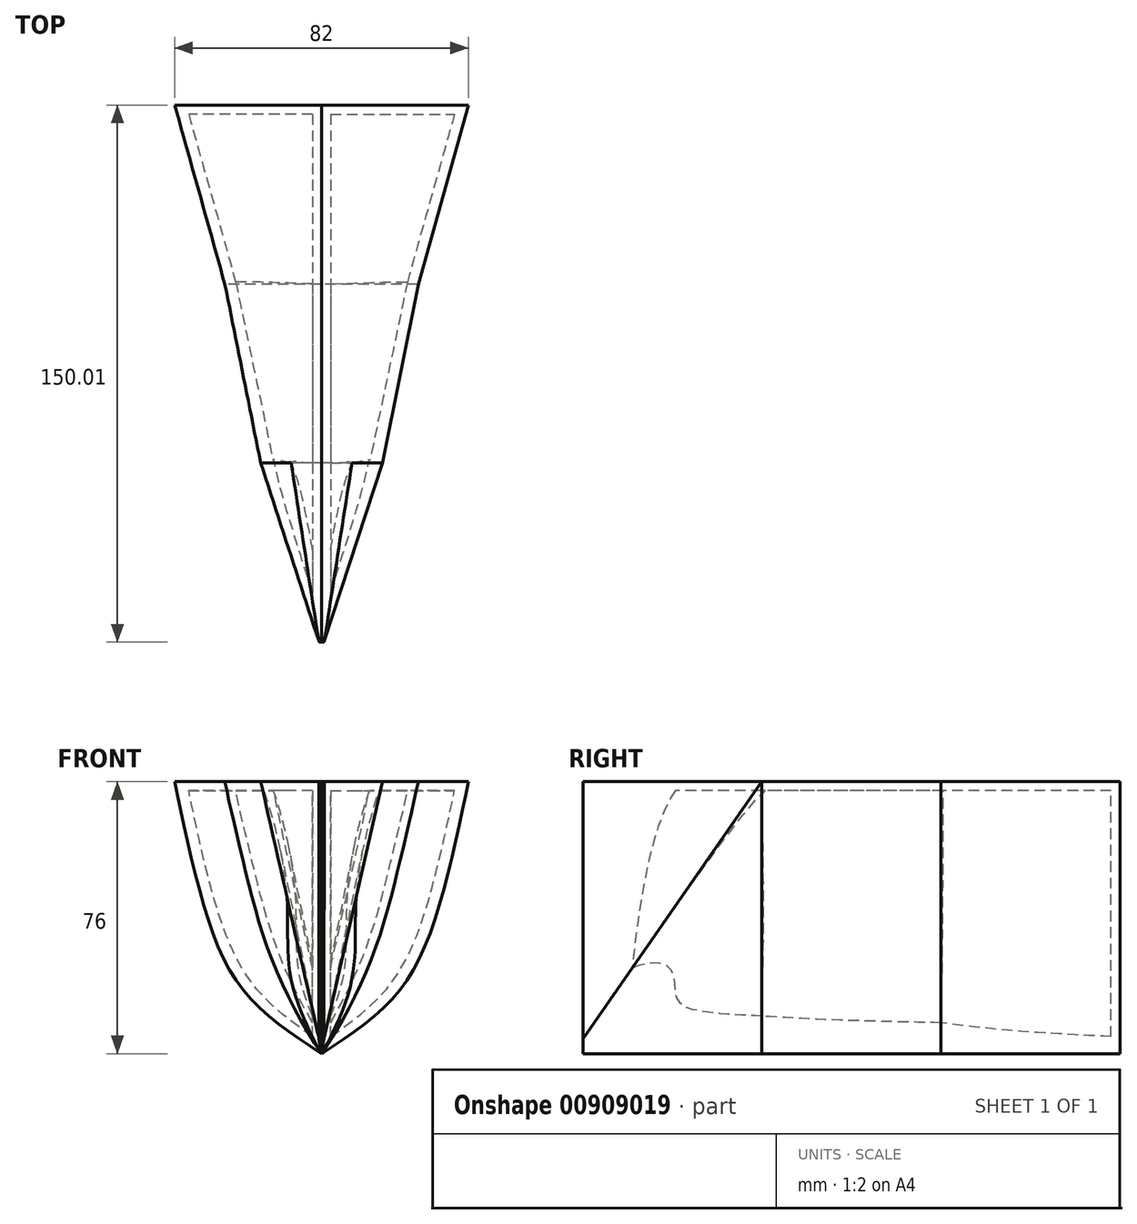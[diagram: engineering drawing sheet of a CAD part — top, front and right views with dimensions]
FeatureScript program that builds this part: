
annotation { "Feature Type Name" : "Feature", "Feature Type Description" : "" }
export const myFeature = defineFeature(function(context is Context, id is Id, definition is map)
    precondition{}
    {
        {
            var Q0;
            Q0=qCreatedBy(makeId("Front.planeOp"),FACE);
            var sketch = newSketch(context, id + "F0", { "sketchPlane" : qUnion([Q0])});
            skLineSegment(sketch, "E0", {"start": v(0, 0) * mm, "end": v(0, 76) * mm});
            skLineSegment(sketch, "E1", {"start": v(0, 76) * mm, "end": v(17, 76) * mm});
            skFitSpline(sketch, "E2", {"points": [v(17, 76) * mm, v(9.77, 45.12) * mm, v(7.96, 18.5) * mm, v(0, 0) * mm], "startDerivative": vector(-25.36, -64.7) * mm, "endDerivative": vector(-12.13, -18.2) * mm});
            skSolve(sketch);
        }
        {
            var Q0;
            Q0=makeQuery(id+"F0.imprint","IMPRINT",FACE,{"disambiguationData":[TD([[makeQuery(id+"F0.imprint","IMPRINT",EDGE,{"derivedFrom":sQuery(id+"F0.wireOp",EDGE,"E0")}),-1.0]])]});
            extrude(context, id + "F1", {"entities" : qUnion([Q0]), "depth" : 0 * mm, "offsetDistance" : 25 * mm});
        }
        {
            var Q0;
            Q0=qCreatedBy(makeId("Front.planeOp"),FACE);
            cPlane(context, id + "F2", {"entities" : qUnion([Q0]), "cplaneType" : CPlaneType.OFFSET, "offset" : 50 * mm, "width" : 150 * mm, "height" : 150 * mm});
        }
        {
            var Q0;
            Q0=qCreatedBy(id+"F2.planeOp",FACE);
            var sketch = newSketch(context, id + "F3", { "sketchPlane" : qUnion([Q0])});
            skLineSegment(sketch, "E3", {"start": v(0, 0) * mm, "end": v(0.69, 4.15) * mm});
            skLineSegment(sketch, "E4", {"start": v(0.69, 4.15) * mm, "end": v(0.75, 76) * mm});
            skLineSegment(sketch, "E5", {"start": v(0.75, 76) * mm, "end": v(0, 76) * mm});
            skLineSegment(sketch, "E6", {"start": v(0, 76) * mm, "end": v(0, 0) * mm});
            skSolve(sketch);
        }
        {
            var Q0;
            Q0=makeQuery(id+"F3.imprint","IMPRINT",FACE,{"disambiguationData":[TD([[makeQuery(id+"F3.imprint","IMPRINT",EDGE,{"derivedFrom":sQuery(id+"F3.wireOp",EDGE,"E3")}),1.0]])]});
            extrude(context, id + "F4", {"entities" : qUnion([Q0]), "depth" : 0.01 * mm, "offsetDistance" : 25 * mm});
        }
        {
            var Q0;
            Q0=makeQuery(id+"F1.opExtrude","CAP_FACE",FACE,{"disambiguationData":[OSD([sQuery(id+"F0.wireOp",EDGE,"E0"),sQuery(id+"F0.wireOp",EDGE,"E1"),sQuery(id+"F0.wireOp",EDGE,"E2")])],"isStart":false});
            var Q1;
            Q1=makeQuery(id+"F4.opExtrude","CAP_FACE",FACE,{"disambiguationData":[OSD([sQuery(id+"F3.wireOp",EDGE,"E3"),sQuery(id+"F3.wireOp",EDGE,"E4"),sQuery(id+"F3.wireOp",EDGE,"E5"),sQuery(id+"F3.wireOp",EDGE,"E6")])],"isStart":true});
            loft(context, id + "F5", {"sheetProfilesArray" : [{ "sheetProfileEntities" : qUnion([Q0]) }, { "sheetProfileEntities" : qUnion([Q1]) }]});
        }
        {
            var Q0;
            Q0=qCreatedBy(makeId("Front.planeOp"),FACE);
            cPlane(context, id + "F6", {"entities" : qUnion([Q0]), "cplaneType" : CPlaneType.OFFSET, "offset" : 50 * mm, "oppositeDirection" : true, "width" : 150 * mm, "height" : 150 * mm});
        }
        {
            var Q0;
            Q0=qCreatedBy(id+"F6.planeOp",FACE);
            var sketch = newSketch(context, id + "F7", { "sketchPlane" : qUnion([Q0])});
            skLineSegment(sketch, "E7", {"start": v(0, 0) * mm, "end": v(0, 76) * mm});
            skLineSegment(sketch, "E8", {"start": v(0, 76) * mm, "end": v(27, 76) * mm});
            skFitSpline(sketch, "E9", {"points": [v(27, 76) * mm, v(22, 54.23) * mm, v(14.03, 26.66) * mm, v(0, 0) * mm], "startDerivative": vector(-11.37, -55.97) * mm, "endDerivative": vector(-46.16, -68.27) * mm});
            skSolve(sketch);
        }
        {
            var Q1;
            Q1=makeQuery(id+"F7.imprint","IMPRINT",FACE,{"disambiguationData":[TD([[makeQuery(id+"F7.imprint","IMPRINT",EDGE,{"derivedFrom":sQuery(id+"F7.wireOp",EDGE,"E7")}),-1.0]])]});
            var Q2;
            Q2=makeQuery(id+"F0.imprint","IMPRINT",FACE,{"disambiguationData":[TD([[makeQuery(id+"F0.imprint","IMPRINT",EDGE,{"derivedFrom":sQuery(id+"F0.wireOp",EDGE,"E0")}),-1.0]])]});
            loft(context, id + "F8", {"operationType" : NewBodyOperationType.ADD, "sheetProfilesArray" : [{ "sheetProfileEntities" : qUnion([Q1]) }, { "sheetProfileEntities" : qUnion([Q2]) }]});
        }
        {
            var Q0;
            Q0=qCreatedBy(id+"F6.planeOp",FACE);
            cPlane(context, id + "F9", {"entities" : qUnion([Q0]), "cplaneType" : CPlaneType.OFFSET, "offset" : 50 * mm, "oppositeDirection" : true, "width" : 150 * mm, "height" : 150 * mm});
        }
        {
            var Q0;
            Q0=qCreatedBy(id+"F9.planeOp",FACE);
            var sketch = newSketch(context, id + "F10", { "sketchPlane" : qUnion([Q0])});
            skLineSegment(sketch, "E10", {"start": v(0, 0) * mm, "end": v(0, 76) * mm});
            skLineSegment(sketch, "E11", {"start": v(0, 76) * mm, "end": v(41, 76) * mm});
            skFitSpline(sketch, "E12", {"points": [v(41, 76) * mm, v(31.99, 38.45) * mm, v(19.8, 15.3) * mm, v(0, 0) * mm], "startDerivative": vector(-17.34, -81.35) * mm, "endDerivative": vector(-70.37, -46.1) * mm});
            skSolve(sketch);
        }
        {
            var Q1;
            Q1=makeQuery(id+"F10.imprint","IMPRINT",FACE,{"disambiguationData":[TD([[makeQuery(id+"F10.imprint","IMPRINT",EDGE,{"derivedFrom":sQuery(id+"F10.wireOp",EDGE,"E10")}),-1.0]])]});
            var Q2;
            Q2=makeQuery(id+"F8.opLoft","CAP_FACE",FACE,{"disambiguationData":[OSD([makeQuery(id+"F7.imprint","IMPRINT",FACE,{"disambiguationData":[TD([[makeQuery(id+"F7.imprint","IMPRINT",EDGE,{"derivedFrom":sQuery(id+"F7.wireOp",EDGE,"E7")}),-1.0]])]})])],"isStart":true});
            loft(context, id + "F11", {"operationType" : NewBodyOperationType.ADD, "sheetProfilesArray" : [{ "sheetProfileEntities" : qUnion([Q1]) }, { "sheetProfileEntities" : qUnion([Q2]) }]});
        }
        {
            var Q0;
            Q0=makeQuery(id+"F1.opExtrude","SWEPT_BODY",BODY,{"disambiguationData":[OSD([sQuery(id+"F0.wireOp",EDGE,"E0"),sQuery(id+"F0.wireOp",EDGE,"E1"),sQuery(id+"F0.wireOp",EDGE,"E2")])]});
            var Q1;
            Q1=makeQuery(id+"F5.opLoft","SWEPT_BODY",BODY,{"disambiguationData":[OSD([sQuery(id+"F0.wireOp",EDGE,"E0"),sQuery(id+"F0.wireOp",EDGE,"E1"),sQuery(id+"F0.wireOp",EDGE,"E2"),sQuery(id+"F3.wireOp",EDGE,"E3"),sQuery(id+"F3.wireOp",EDGE,"E4"),sQuery(id+"F3.wireOp",EDGE,"E5"),sQuery(id+"F3.wireOp",EDGE,"E6")])]});
            var Q2;
            Q2=makeQuery(id+"F4.opExtrude","SWEPT_BODY",BODY,{"disambiguationData":[OSD([sQuery(id+"F3.wireOp",EDGE,"E3"),sQuery(id+"F3.wireOp",EDGE,"E4"),sQuery(id+"F3.wireOp",EDGE,"E5"),sQuery(id+"F3.wireOp",EDGE,"E6")])]});
            var Q3;
            Q3=makeQuery(id+"F5.opLoft","SWEPT_FACE",FACE,{"disambiguationData":[OSD([sQuery(id+"F0.wireOp",EDGE,"E0"),sQuery(id+"F0.wireOp",EDGE,"E1"),sQuery(id+"F0.wireOp",EDGE,"E2"),sQuery(id+"F3.wireOp",EDGE,"E3"),sQuery(id+"F3.wireOp",EDGE,"E5"),sQuery(id+"F3.wireOp",EDGE,"E6")])]});
            mirror(context, id + "F12", {"entities" : qUnion([Q0, Q1, Q2]), "mirrorPlane" : qUnion([Q3])});
        }
        {
            var Q0;
            Q0=makeQuery(id+"F11.opLoft","CAP_FACE",FACE,{"disambiguationData":[OSD([makeQuery(id+"F10.imprint","IMPRINT",FACE,{"disambiguationData":[TD([[makeQuery(id+"F10.imprint","IMPRINT",EDGE,{"derivedFrom":sQuery(id+"F10.wireOp",EDGE,"E10")}),-1.0]])]})])],"isStart":true});
            var Q1;
            {var subQ0=sQuery(id+"F10.wireOp",EDGE,"E12");var subQ1=sQuery(id+"F10.wireOp",EDGE,"E11");var subQ2=sQuery(id+"F10.wireOp",EDGE,"E10");var subQ3=sQuery(id+"F7.wireOp",EDGE,"E9");var subQ4=sQuery(id+"F7.wireOp",EDGE,"E8");var subQ5=sQuery(id+"F7.wireOp",EDGE,"E7");Q1=makeQuery(id+"F11.opLoft","SWEPT_FACE",FACE,{"disambiguationData":[OSD([subQ5,subQ4,subQ3,subQ2,subQ1,subQ0]),TDD([makeQuery(id+"F8.opLoft","MID_CAP_VERTEX",VERTEX,{"disambiguationData":[OSD([subQ5,subQ3])],"capPos":0.0}),makeQuery(id+"F8.opLoft","MID_CAP_VERTEX",VERTEX,{"disambiguationData":[OSD([subQ4,subQ3])],"capPos":0.0}),makeQuery(id+"F8.opLoft","MID_CAP_EDGE",EDGE,{"disambiguationData":[OSD([subQ5,subQ4,subQ3]),TDD([makeQuery(id+"F7.imprint","INTERSECT",VERTEX,{"derivedFrom":[subQ5,subQ3]}),makeQuery(id+"F7.imprint","INTERSECT",VERTEX,{"derivedFrom":[subQ4,subQ3]}),makeQuery(id+"F7.imprint","IMPRINT",EDGE,{"derivedFrom":subQ3})])],"capPos":0.0}),makeQuery(id+"F10.imprint","INTERSECT",VERTEX,{"derivedFrom":[subQ2,subQ0]}),makeQuery(id+"F10.imprint","INTERSECT",VERTEX,{"derivedFrom":[subQ1,subQ0]}),makeQuery(id+"F10.imprint","IMPRINT",EDGE,{"derivedFrom":subQ0})])]});}
            var Q2;
            {var subQ0=sQuery(id+"F7.wireOp",EDGE,"E9");var subQ1=sQuery(id+"F7.wireOp",EDGE,"E8");var subQ2=sQuery(id+"F7.wireOp",EDGE,"E7");var subQ3=sQuery(id+"F0.wireOp",EDGE,"E2");var subQ4=sQuery(id+"F0.wireOp",EDGE,"E1");var subQ5=sQuery(id+"F0.wireOp",EDGE,"E0");Q2=makeQuery(id+"F8.opLoft","SWEPT_FACE",FACE,{"disambiguationData":[OSD([subQ5,subQ4,subQ3,subQ2,subQ1,subQ0]),TDD([makeQuery(id+"F0.imprint","INTERSECT",VERTEX,{"derivedFrom":[subQ5,subQ3]}),makeQuery(id+"F0.imprint","INTERSECT",VERTEX,{"derivedFrom":[subQ4,subQ3]}),makeQuery(id+"F0.imprint","IMPRINT",EDGE,{"derivedFrom":subQ3}),makeQuery(id+"F7.imprint","INTERSECT",VERTEX,{"derivedFrom":[subQ2,subQ0]}),makeQuery(id+"F7.imprint","INTERSECT",VERTEX,{"derivedFrom":[subQ1,subQ0]}),makeQuery(id+"F7.imprint","IMPRINT",EDGE,{"derivedFrom":subQ0})])]});}
            var Q3;
            {var subQ0=sQuery(id+"F10.wireOp",EDGE,"E11");var subQ1=sQuery(id+"F10.wireOp",EDGE,"E12");var subQ2=sQuery(id+"F10.wireOp",EDGE,"E10");var subQ3=sQuery(id+"F7.wireOp",EDGE,"E8");var subQ4=makeQuery(id+"F7.imprint","IMPRINT",EDGE,{"derivedFrom":subQ3});var subQ5=sQuery(id+"F7.wireOp",EDGE,"E9");var subQ6=makeQuery(id+"F7.imprint","INTERSECT",VERTEX,{"derivedFrom":[subQ3,subQ5]});var subQ7=sQuery(id+"F7.wireOp",EDGE,"E7");var subQ8=makeQuery(id+"F7.imprint","INTERSECT",VERTEX,{"derivedFrom":[subQ7,subQ3]});var subQ9=sQuery(id+"F0.wireOp",EDGE,"E1");var subQ10=sQuery(id+"F0.wireOp",EDGE,"E2");var subQ11=sQuery(id+"F0.wireOp",EDGE,"E0");Q3=makeQuery(id+"F11.boolean.opBoolean","MERGE",FACE,{"derivedFrom":[makeQuery(id+"F8.boolean.opBoolean","MERGE",FACE,{"derivedFrom":[makeQuery(id+"F1.opExtrude","SWEPT_FACE",FACE,{"disambiguationData":[OSD([subQ9])]}),makeQuery(id+"F8.opLoft","SWEPT_FACE",FACE,{"disambiguationData":[OSD([subQ11,subQ9,subQ10,subQ7,subQ3,subQ5]),TDD([makeQuery(id+"F0.imprint","INTERSECT",VERTEX,{"derivedFrom":[subQ11,subQ9]}),makeQuery(id+"F0.imprint","INTERSECT",VERTEX,{"derivedFrom":[subQ9,subQ10]}),makeQuery(id+"F0.imprint","IMPRINT",EDGE,{"derivedFrom":subQ9}),subQ8,subQ6,subQ4])]})]}),makeQuery(id+"F11.opLoft","SWEPT_FACE",FACE,{"disambiguationData":[OSD([subQ7,subQ3,subQ5,subQ2,subQ0,subQ1]),TDD([makeQuery(id+"F8.opLoft","MID_CAP_VERTEX",VERTEX,{"disambiguationData":[OSD([subQ7,subQ3])],"capPos":0.0}),makeQuery(id+"F8.opLoft","MID_CAP_VERTEX",VERTEX,{"disambiguationData":[OSD([subQ3,subQ5])],"capPos":0.0}),makeQuery(id+"F8.opLoft","MID_CAP_EDGE",EDGE,{"disambiguationData":[OSD([subQ7,subQ3,subQ5]),TDD([subQ8,subQ6,subQ4])],"capPos":0.0}),makeQuery(id+"F10.imprint","INTERSECT",VERTEX,{"derivedFrom":[subQ2,subQ0]}),makeQuery(id+"F10.imprint","INTERSECT",VERTEX,{"derivedFrom":[subQ0,subQ1]}),makeQuery(id+"F10.imprint","IMPRINT",EDGE,{"derivedFrom":subQ0})])]})]});}
            var Q4;
            Q4=makeQuery(id+"F5.opLoft","SWEPT_FACE",FACE,{"disambiguationData":[OSD([sQuery(id+"F0.wireOp",EDGE,"E0"),sQuery(id+"F0.wireOp",EDGE,"E1"),sQuery(id+"F0.wireOp",EDGE,"E2"),sQuery(id+"F3.wireOp",EDGE,"E4"),sQuery(id+"F3.wireOp",EDGE,"E5"),sQuery(id+"F3.wireOp",EDGE,"E6")])]});
            var Q5;
            Q5=makeQuery(id+"F5.opLoft","SWEPT_FACE",FACE,{"disambiguationData":[OSD([sQuery(id+"F0.wireOp",EDGE,"E1"),sQuery(id+"F0.wireOp",EDGE,"E2"),sQuery(id+"F3.wireOp",EDGE,"E3"),sQuery(id+"F3.wireOp",EDGE,"E4"),sQuery(id+"F3.wireOp",EDGE,"E5"),sQuery(id+"F3.wireOp",EDGE,"E6")])]});
            var Q6;
            Q6=makeQuery(id+"F12.opPattern","COPY",FACE,{"derivedFrom":makeQuery(id+"F11.opLoft","CAP_FACE",FACE,{"disambiguationData":[OSD([makeQuery(id+"F10.imprint","IMPRINT",FACE,{"disambiguationData":[TD([[makeQuery(id+"F10.imprint","IMPRINT",EDGE,{"derivedFrom":sQuery(id+"F10.wireOp",EDGE,"E10")}),-1.0]])]})])],"isStart":true}),"instanceName":"1"});
            var Q7;
            {var subQ0=sQuery(id+"F7.wireOp",EDGE,"E9");var subQ1=sQuery(id+"F7.wireOp",EDGE,"E8");var subQ2=sQuery(id+"F7.wireOp",EDGE,"E7");var subQ3=sQuery(id+"F0.wireOp",EDGE,"E2");var subQ4=sQuery(id+"F0.wireOp",EDGE,"E1");var subQ5=sQuery(id+"F0.wireOp",EDGE,"E0");Q7=makeQuery(id+"F12.opPattern","COPY",FACE,{"derivedFrom":makeQuery(id+"F8.opLoft","SWEPT_FACE",FACE,{"disambiguationData":[OSD([subQ5,subQ4,subQ3,subQ2,subQ1,subQ0]),TDD([makeQuery(id+"F0.imprint","INTERSECT",VERTEX,{"derivedFrom":[subQ5,subQ3]}),makeQuery(id+"F0.imprint","INTERSECT",VERTEX,{"derivedFrom":[subQ4,subQ3]}),makeQuery(id+"F0.imprint","IMPRINT",EDGE,{"derivedFrom":subQ3}),makeQuery(id+"F7.imprint","INTERSECT",VERTEX,{"derivedFrom":[subQ2,subQ0]}),makeQuery(id+"F7.imprint","INTERSECT",VERTEX,{"derivedFrom":[subQ1,subQ0]}),makeQuery(id+"F7.imprint","IMPRINT",EDGE,{"derivedFrom":subQ0})])]}),"instanceName":"1"});}
            var Q8;
            {var subQ0=sQuery(id+"F10.wireOp",EDGE,"E12");var subQ1=sQuery(id+"F10.wireOp",EDGE,"E11");var subQ2=sQuery(id+"F10.wireOp",EDGE,"E10");var subQ3=sQuery(id+"F7.wireOp",EDGE,"E9");var subQ4=sQuery(id+"F7.wireOp",EDGE,"E8");var subQ5=sQuery(id+"F7.wireOp",EDGE,"E7");Q8=makeQuery(id+"F12.opPattern","COPY",FACE,{"derivedFrom":makeQuery(id+"F11.opLoft","SWEPT_FACE",FACE,{"disambiguationData":[OSD([subQ5,subQ4,subQ3,subQ2,subQ1,subQ0]),TDD([makeQuery(id+"F8.opLoft","MID_CAP_VERTEX",VERTEX,{"disambiguationData":[OSD([subQ5,subQ3])],"capPos":0.0}),makeQuery(id+"F8.opLoft","MID_CAP_VERTEX",VERTEX,{"disambiguationData":[OSD([subQ4,subQ3])],"capPos":0.0}),makeQuery(id+"F8.opLoft","MID_CAP_EDGE",EDGE,{"disambiguationData":[OSD([subQ5,subQ4,subQ3]),TDD([makeQuery(id+"F7.imprint","INTERSECT",VERTEX,{"derivedFrom":[subQ5,subQ3]}),makeQuery(id+"F7.imprint","INTERSECT",VERTEX,{"derivedFrom":[subQ4,subQ3]}),makeQuery(id+"F7.imprint","IMPRINT",EDGE,{"derivedFrom":subQ3})])],"capPos":0.0}),makeQuery(id+"F10.imprint","INTERSECT",VERTEX,{"derivedFrom":[subQ2,subQ0]}),makeQuery(id+"F10.imprint","INTERSECT",VERTEX,{"derivedFrom":[subQ1,subQ0]}),makeQuery(id+"F10.imprint","IMPRINT",EDGE,{"derivedFrom":subQ0})])]}),"instanceName":"1"});}
            var Q9;
            Q9=makeQuery(id+"F12.opPattern","COPY",FACE,{"derivedFrom":makeQuery(id+"F1.opExtrude","CAP_FACE",FACE,{"disambiguationData":[OSD([sQuery(id+"F0.wireOp",EDGE,"E0"),sQuery(id+"F0.wireOp",EDGE,"E1"),sQuery(id+"F0.wireOp",EDGE,"E2")])],"isStart":false}),"instanceName":"1"});
            var Q10;
            {var subQ0=sQuery(id+"F10.wireOp",EDGE,"E10");var subQ1=sQuery(id+"F10.wireOp",EDGE,"E11");var subQ2=sQuery(id+"F10.wireOp",EDGE,"E12");var subQ3=sQuery(id+"F7.wireOp",EDGE,"E7");var subQ4=makeQuery(id+"F7.imprint","IMPRINT",EDGE,{"derivedFrom":subQ3});var subQ5=sQuery(id+"F7.wireOp",EDGE,"E8");var subQ6=makeQuery(id+"F7.imprint","INTERSECT",VERTEX,{"derivedFrom":[subQ3,subQ5]});var subQ7=sQuery(id+"F7.wireOp",EDGE,"E9");var subQ8=makeQuery(id+"F7.imprint","INTERSECT",VERTEX,{"derivedFrom":[subQ3,subQ7]});var subQ9=sQuery(id+"F0.wireOp",EDGE,"E0");var subQ10=sQuery(id+"F0.wireOp",EDGE,"E1");var subQ11=sQuery(id+"F0.wireOp",EDGE,"E2");Q10=makeQuery(id+"F12.opPattern","COPY",FACE,{"derivedFrom":makeQuery(id+"F11.boolean.opBoolean","MERGE",FACE,{"derivedFrom":[makeQuery(id+"F8.boolean.opBoolean","MERGE",FACE,{"derivedFrom":[makeQuery(id+"F1.opExtrude","SWEPT_FACE",FACE,{"disambiguationData":[OSD([subQ9])]}),makeQuery(id+"F8.opLoft","SWEPT_FACE",FACE,{"disambiguationData":[OSD([subQ9,subQ10,subQ11,subQ3,subQ5,subQ7]),TDD([makeQuery(id+"F0.imprint","INTERSECT",VERTEX,{"derivedFrom":[subQ9,subQ11]}),makeQuery(id+"F0.imprint","INTERSECT",VERTEX,{"derivedFrom":[subQ9,subQ10]}),makeQuery(id+"F0.imprint","IMPRINT",EDGE,{"derivedFrom":subQ9}),subQ8,subQ6,subQ4])]})]}),makeQuery(id+"F11.opLoft","SWEPT_FACE",FACE,{"disambiguationData":[OSD([subQ3,subQ5,subQ7,subQ0,subQ1,subQ2]),TDD([makeQuery(id+"F8.opLoft","MID_CAP_VERTEX",VERTEX,{"disambiguationData":[OSD([subQ3,subQ7])],"capPos":0.0}),makeQuery(id+"F8.opLoft","MID_CAP_VERTEX",VERTEX,{"disambiguationData":[OSD([subQ3,subQ5])],"capPos":0.0}),makeQuery(id+"F8.opLoft","MID_CAP_EDGE",EDGE,{"disambiguationData":[OSD([subQ3,subQ5,subQ7]),TDD([subQ8,subQ6,subQ4])],"capPos":0.0}),makeQuery(id+"F10.imprint","INTERSECT",VERTEX,{"derivedFrom":[subQ0,subQ2]}),makeQuery(id+"F10.imprint","INTERSECT",VERTEX,{"derivedFrom":[subQ0,subQ1]}),makeQuery(id+"F10.imprint","IMPRINT",EDGE,{"derivedFrom":subQ0})])]})]}),"instanceName":"1"});}
            var Q11;
            {var subQ0=sQuery(id+"F10.wireOp",EDGE,"E11");var subQ1=sQuery(id+"F10.wireOp",EDGE,"E12");var subQ2=sQuery(id+"F10.wireOp",EDGE,"E10");var subQ3=sQuery(id+"F7.wireOp",EDGE,"E8");var subQ4=makeQuery(id+"F7.imprint","IMPRINT",EDGE,{"derivedFrom":subQ3});var subQ5=sQuery(id+"F7.wireOp",EDGE,"E9");var subQ6=makeQuery(id+"F7.imprint","INTERSECT",VERTEX,{"derivedFrom":[subQ3,subQ5]});var subQ7=sQuery(id+"F7.wireOp",EDGE,"E7");var subQ8=makeQuery(id+"F7.imprint","INTERSECT",VERTEX,{"derivedFrom":[subQ7,subQ3]});var subQ9=sQuery(id+"F0.wireOp",EDGE,"E1");var subQ10=sQuery(id+"F0.wireOp",EDGE,"E2");var subQ11=sQuery(id+"F0.wireOp",EDGE,"E0");Q11=makeQuery(id+"F12.opPattern","COPY",FACE,{"derivedFrom":makeQuery(id+"F11.boolean.opBoolean","MERGE",FACE,{"derivedFrom":[makeQuery(id+"F8.boolean.opBoolean","MERGE",FACE,{"derivedFrom":[makeQuery(id+"F1.opExtrude","SWEPT_FACE",FACE,{"disambiguationData":[OSD([subQ9])]}),makeQuery(id+"F8.opLoft","SWEPT_FACE",FACE,{"disambiguationData":[OSD([subQ11,subQ9,subQ10,subQ7,subQ3,subQ5]),TDD([makeQuery(id+"F0.imprint","INTERSECT",VERTEX,{"derivedFrom":[subQ11,subQ9]}),makeQuery(id+"F0.imprint","INTERSECT",VERTEX,{"derivedFrom":[subQ9,subQ10]}),makeQuery(id+"F0.imprint","IMPRINT",EDGE,{"derivedFrom":subQ9}),subQ8,subQ6,subQ4])]})]}),makeQuery(id+"F11.opLoft","SWEPT_FACE",FACE,{"disambiguationData":[OSD([subQ7,subQ3,subQ5,subQ2,subQ0,subQ1]),TDD([makeQuery(id+"F8.opLoft","MID_CAP_VERTEX",VERTEX,{"disambiguationData":[OSD([subQ7,subQ3])],"capPos":0.0}),makeQuery(id+"F8.opLoft","MID_CAP_VERTEX",VERTEX,{"disambiguationData":[OSD([subQ3,subQ5])],"capPos":0.0}),makeQuery(id+"F8.opLoft","MID_CAP_EDGE",EDGE,{"disambiguationData":[OSD([subQ7,subQ3,subQ5]),TDD([subQ8,subQ6,subQ4])],"capPos":0.0}),makeQuery(id+"F10.imprint","INTERSECT",VERTEX,{"derivedFrom":[subQ2,subQ0]}),makeQuery(id+"F10.imprint","INTERSECT",VERTEX,{"derivedFrom":[subQ0,subQ1]}),makeQuery(id+"F10.imprint","IMPRINT",EDGE,{"derivedFrom":subQ0})])]})]}),"instanceName":"1"});}
            var Q12;
            Q12=makeQuery(id+"F12.opPattern","COPY",FACE,{"derivedFrom":makeQuery(id+"F4.opExtrude","CAP_FACE",FACE,{"disambiguationData":[OSD([sQuery(id+"F3.wireOp",EDGE,"E3"),sQuery(id+"F3.wireOp",EDGE,"E4"),sQuery(id+"F3.wireOp",EDGE,"E5"),sQuery(id+"F3.wireOp",EDGE,"E6")])],"isStart":false}),"instanceName":"1"});
            var Q13;
            Q13=makeQuery(id+"F12.opPattern","COPY",FACE,{"derivedFrom":makeQuery(id+"F5.opLoft","SWEPT_FACE",FACE,{"disambiguationData":[OSD([sQuery(id+"F0.wireOp",EDGE,"E0"),sQuery(id+"F0.wireOp",EDGE,"E2"),sQuery(id+"F3.wireOp",EDGE,"E3"),sQuery(id+"F3.wireOp",EDGE,"E4"),sQuery(id+"F3.wireOp",EDGE,"E6")])]}),"instanceName":"1"});
            var Q14;
            Q14=makeQuery(id+"F12.opPattern","COPY",FACE,{"derivedFrom":makeQuery(id+"F5.opLoft","SWEPT_FACE",FACE,{"disambiguationData":[OSD([sQuery(id+"F0.wireOp",EDGE,"E0"),sQuery(id+"F0.wireOp",EDGE,"E1"),sQuery(id+"F0.wireOp",EDGE,"E2"),sQuery(id+"F3.wireOp",EDGE,"E4"),sQuery(id+"F3.wireOp",EDGE,"E5"),sQuery(id+"F3.wireOp",EDGE,"E6")])]}),"instanceName":"1"});
            var Q15;
            Q15=makeQuery(id+"F12.opPattern","COPY",FACE,{"derivedFrom":makeQuery(id+"F5.opLoft","SWEPT_FACE",FACE,{"disambiguationData":[OSD([sQuery(id+"F0.wireOp",EDGE,"E1"),sQuery(id+"F0.wireOp",EDGE,"E2"),sQuery(id+"F3.wireOp",EDGE,"E3"),sQuery(id+"F3.wireOp",EDGE,"E4"),sQuery(id+"F3.wireOp",EDGE,"E5"),sQuery(id+"F3.wireOp",EDGE,"E6")])]}),"instanceName":"1"});
            var Q16;
            Q16=makeQuery(id+"F12.opPattern","COPY",FACE,{"derivedFrom":makeQuery(id+"F5.opLoft","CAP_FACE",FACE,{"disambiguationData":[OSD([sQuery(id+"F0.wireOp",EDGE,"E0"),sQuery(id+"F0.wireOp",EDGE,"E1"),sQuery(id+"F0.wireOp",EDGE,"E2")])],"isStart":true}),"instanceName":"1"});
            var Q17;
            Q17=makeQuery(id+"F1.opExtrude","CAP_FACE",FACE,{"disambiguationData":[OSD([sQuery(id+"F0.wireOp",EDGE,"E0"),sQuery(id+"F0.wireOp",EDGE,"E1"),sQuery(id+"F0.wireOp",EDGE,"E2")])],"isStart":false});
            var Q18;
            {var subQ0=sQuery(id+"F10.wireOp",EDGE,"E10");var subQ1=sQuery(id+"F10.wireOp",EDGE,"E11");var subQ2=sQuery(id+"F10.wireOp",EDGE,"E12");var subQ3=sQuery(id+"F7.wireOp",EDGE,"E7");var subQ4=makeQuery(id+"F7.imprint","IMPRINT",EDGE,{"derivedFrom":subQ3});var subQ5=sQuery(id+"F7.wireOp",EDGE,"E8");var subQ6=makeQuery(id+"F7.imprint","INTERSECT",VERTEX,{"derivedFrom":[subQ3,subQ5]});var subQ7=sQuery(id+"F7.wireOp",EDGE,"E9");var subQ8=makeQuery(id+"F7.imprint","INTERSECT",VERTEX,{"derivedFrom":[subQ3,subQ7]});var subQ9=sQuery(id+"F0.wireOp",EDGE,"E0");var subQ10=sQuery(id+"F0.wireOp",EDGE,"E1");var subQ11=sQuery(id+"F0.wireOp",EDGE,"E2");Q18=makeQuery(id+"F11.boolean.opBoolean","MERGE",FACE,{"derivedFrom":[makeQuery(id+"F8.boolean.opBoolean","MERGE",FACE,{"derivedFrom":[makeQuery(id+"F1.opExtrude","SWEPT_FACE",FACE,{"disambiguationData":[OSD([subQ9])]}),makeQuery(id+"F8.opLoft","SWEPT_FACE",FACE,{"disambiguationData":[OSD([subQ9,subQ10,subQ11,subQ3,subQ5,subQ7]),TDD([makeQuery(id+"F0.imprint","INTERSECT",VERTEX,{"derivedFrom":[subQ9,subQ11]}),makeQuery(id+"F0.imprint","INTERSECT",VERTEX,{"derivedFrom":[subQ9,subQ10]}),makeQuery(id+"F0.imprint","IMPRINT",EDGE,{"derivedFrom":subQ9}),subQ8,subQ6,subQ4])]})]}),makeQuery(id+"F11.opLoft","SWEPT_FACE",FACE,{"disambiguationData":[OSD([subQ3,subQ5,subQ7,subQ0,subQ1,subQ2]),TDD([makeQuery(id+"F8.opLoft","MID_CAP_VERTEX",VERTEX,{"disambiguationData":[OSD([subQ3,subQ7])],"capPos":0.0}),makeQuery(id+"F8.opLoft","MID_CAP_VERTEX",VERTEX,{"disambiguationData":[OSD([subQ3,subQ5])],"capPos":0.0}),makeQuery(id+"F8.opLoft","MID_CAP_EDGE",EDGE,{"disambiguationData":[OSD([subQ3,subQ5,subQ7]),TDD([subQ8,subQ6,subQ4])],"capPos":0.0}),makeQuery(id+"F10.imprint","INTERSECT",VERTEX,{"derivedFrom":[subQ0,subQ2]}),makeQuery(id+"F10.imprint","INTERSECT",VERTEX,{"derivedFrom":[subQ0,subQ1]}),makeQuery(id+"F10.imprint","IMPRINT",EDGE,{"derivedFrom":subQ0})])]})]});}
            var Q19;
            Q19=makeQuery(id+"F5.opLoft","CAP_FACE",FACE,{"disambiguationData":[OSD([sQuery(id+"F0.wireOp",EDGE,"E0"),sQuery(id+"F0.wireOp",EDGE,"E1"),sQuery(id+"F0.wireOp",EDGE,"E2")])],"isStart":true});
            var Q20;
            Q20=makeQuery(id+"F5.opLoft","SWEPT_FACE",FACE,{"disambiguationData":[OSD([sQuery(id+"F0.wireOp",EDGE,"E0"),sQuery(id+"F0.wireOp",EDGE,"E2"),sQuery(id+"F3.wireOp",EDGE,"E3"),sQuery(id+"F3.wireOp",EDGE,"E4"),sQuery(id+"F3.wireOp",EDGE,"E6")])]});
            var Q21;
            Q21=makeQuery(id+"F5.opLoft","SWEPT_FACE",FACE,{"disambiguationData":[OSD([sQuery(id+"F0.wireOp",EDGE,"E0"),sQuery(id+"F0.wireOp",EDGE,"E1"),sQuery(id+"F0.wireOp",EDGE,"E2"),sQuery(id+"F3.wireOp",EDGE,"E3"),sQuery(id+"F3.wireOp",EDGE,"E5"),sQuery(id+"F3.wireOp",EDGE,"E6")])]});
            var Q22;
            Q22=makeQuery(id+"F12.opPattern","COPY",FACE,{"derivedFrom":makeQuery(id+"F4.opExtrude","SWEPT_FACE",FACE,{"disambiguationData":[OSD([sQuery(id+"F3.wireOp",EDGE,"E4")])]}),"instanceName":"1"});
            var Q23;
            Q23=makeQuery(id+"F12.opPattern","COPY",FACE,{"derivedFrom":makeQuery(id+"F5.opLoft","SWEPT_FACE",FACE,{"disambiguationData":[OSD([sQuery(id+"F0.wireOp",EDGE,"E0"),sQuery(id+"F0.wireOp",EDGE,"E1"),sQuery(id+"F0.wireOp",EDGE,"E2"),sQuery(id+"F3.wireOp",EDGE,"E3"),sQuery(id+"F3.wireOp",EDGE,"E5"),sQuery(id+"F3.wireOp",EDGE,"E6")])]}),"instanceName":"1"});
            var Q24;
            Q24=makeQuery(id+"F12.opPattern","COPY",FACE,{"derivedFrom":makeQuery(id+"F4.opExtrude","SWEPT_FACE",FACE,{"disambiguationData":[OSD([sQuery(id+"F3.wireOp",EDGE,"E3")])]}),"instanceName":"1"});
            var Q25;
            Q25=makeQuery(id+"F12.opPattern","COPY",FACE,{"derivedFrom":makeQuery(id+"F5.opLoft","CAP_FACE",FACE,{"disambiguationData":[OSD([sQuery(id+"F3.wireOp",EDGE,"E3"),sQuery(id+"F3.wireOp",EDGE,"E4"),sQuery(id+"F3.wireOp",EDGE,"E5"),sQuery(id+"F3.wireOp",EDGE,"E6")])],"isStart":true}),"instanceName":"1"});
            var Q26;
            Q26=makeQuery(id+"F4.opExtrude","SWEPT_FACE",FACE,{"disambiguationData":[OSD([sQuery(id+"F3.wireOp",EDGE,"E6")])]});
            var Q27;
            Q27=makeQuery(id+"F12.opPattern","COPY",FACE,{"derivedFrom":makeQuery(id+"F4.opExtrude","CAP_FACE",FACE,{"disambiguationData":[OSD([sQuery(id+"F3.wireOp",EDGE,"E3"),sQuery(id+"F3.wireOp",EDGE,"E4"),sQuery(id+"F3.wireOp",EDGE,"E5"),sQuery(id+"F3.wireOp",EDGE,"E6")])],"isStart":true}),"instanceName":"1"});
            var Q28;
            Q28=makeQuery(id+"F12.opPattern","COPY",FACE,{"derivedFrom":makeQuery(id+"F4.opExtrude","SWEPT_FACE",FACE,{"disambiguationData":[OSD([sQuery(id+"F3.wireOp",EDGE,"E6")])]}),"instanceName":"1"});
            var Q29;
            Q29=makeQuery(id+"F4.opExtrude","CAP_FACE",FACE,{"disambiguationData":[OSD([sQuery(id+"F3.wireOp",EDGE,"E3"),sQuery(id+"F3.wireOp",EDGE,"E4"),sQuery(id+"F3.wireOp",EDGE,"E5"),sQuery(id+"F3.wireOp",EDGE,"E6")])],"isStart":true});
            var Q30;
            Q30=makeQuery(id+"F4.opExtrude","CAP_FACE",FACE,{"disambiguationData":[OSD([sQuery(id+"F3.wireOp",EDGE,"E3"),sQuery(id+"F3.wireOp",EDGE,"E4"),sQuery(id+"F3.wireOp",EDGE,"E5"),sQuery(id+"F3.wireOp",EDGE,"E6")])],"isStart":false});
            var Q31;
            Q31=makeQuery(id+"F4.opExtrude","SWEPT_FACE",FACE,{"disambiguationData":[OSD([sQuery(id+"F3.wireOp",EDGE,"E3")])]});
            var Q32;
            Q32=makeQuery(id+"F5.opLoft","CAP_FACE",FACE,{"disambiguationData":[OSD([sQuery(id+"F3.wireOp",EDGE,"E3"),sQuery(id+"F3.wireOp",EDGE,"E4"),sQuery(id+"F3.wireOp",EDGE,"E5"),sQuery(id+"F3.wireOp",EDGE,"E6")])],"isStart":true});
            var Q33;
            Q33=makeQuery(id+"F12.opPattern","COPY",FACE,{"derivedFrom":makeQuery(id+"F4.opExtrude","SWEPT_FACE",FACE,{"disambiguationData":[OSD([sQuery(id+"F3.wireOp",EDGE,"E5")])]}),"instanceName":"1"});
            var Q34;
            Q34=makeQuery(id+"F4.opExtrude","SWEPT_FACE",FACE,{"disambiguationData":[OSD([sQuery(id+"F3.wireOp",EDGE,"E4")])]});
            var Q35;
            Q35=makeQuery(id+"F4.opExtrude","SWEPT_FACE",FACE,{"disambiguationData":[OSD([sQuery(id+"F3.wireOp",EDGE,"E5")])]});
            var Q36;
            Q36=makeQuery(id+"F12.opPattern","COPY",BODY,{"derivedFrom":makeQuery(id+"F1.opExtrude","SWEPT_BODY",BODY,{"disambiguationData":[OSD([sQuery(id+"F0.wireOp",EDGE,"E0"),sQuery(id+"F0.wireOp",EDGE,"E1"),sQuery(id+"F0.wireOp",EDGE,"E2")])]}),"instanceName":"1"});
            var Q37;
            Q37=makeQuery(id+"F1.opExtrude","SWEPT_BODY",BODY,{"disambiguationData":[OSD([sQuery(id+"F0.wireOp",EDGE,"E0"),sQuery(id+"F0.wireOp",EDGE,"E1"),sQuery(id+"F0.wireOp",EDGE,"E2")])]});
            var Q38;
            Q38=makeQuery(id+"F5.opLoft","SWEPT_BODY",BODY,{"disambiguationData":[OSD([sQuery(id+"F0.wireOp",EDGE,"E0"),sQuery(id+"F0.wireOp",EDGE,"E1"),sQuery(id+"F0.wireOp",EDGE,"E2"),sQuery(id+"F3.wireOp",EDGE,"E3"),sQuery(id+"F3.wireOp",EDGE,"E4"),sQuery(id+"F3.wireOp",EDGE,"E5"),sQuery(id+"F3.wireOp",EDGE,"E6")])]});
            var Q39;
            Q39=makeQuery(id+"F12.opPattern","COPY",BODY,{"derivedFrom":makeQuery(id+"F5.opLoft","SWEPT_BODY",BODY,{"disambiguationData":[OSD([sQuery(id+"F0.wireOp",EDGE,"E0"),sQuery(id+"F0.wireOp",EDGE,"E1"),sQuery(id+"F0.wireOp",EDGE,"E2"),sQuery(id+"F3.wireOp",EDGE,"E3"),sQuery(id+"F3.wireOp",EDGE,"E4"),sQuery(id+"F3.wireOp",EDGE,"E5"),sQuery(id+"F3.wireOp",EDGE,"E6")])]}),"instanceName":"1"});
            shell(context, id + "F13", {"isHollow" : true, "entities" : qUnion([Q0, Q1, Q2, Q3, Q4, Q5, Q6, Q7, Q8, Q9, Q10, Q11, Q12, Q13, Q14, Q15, Q16, Q17, Q18, Q19, Q20, Q21, Q22, Q23, Q24, Q25, Q26, Q27, Q28, Q29, Q30, Q31, Q32, Q33, Q34, Q35]), "parts" : qUnion([Q36, Q37, Q38, Q39]), "thickness" : 2.5 * mm});
        }
    });
